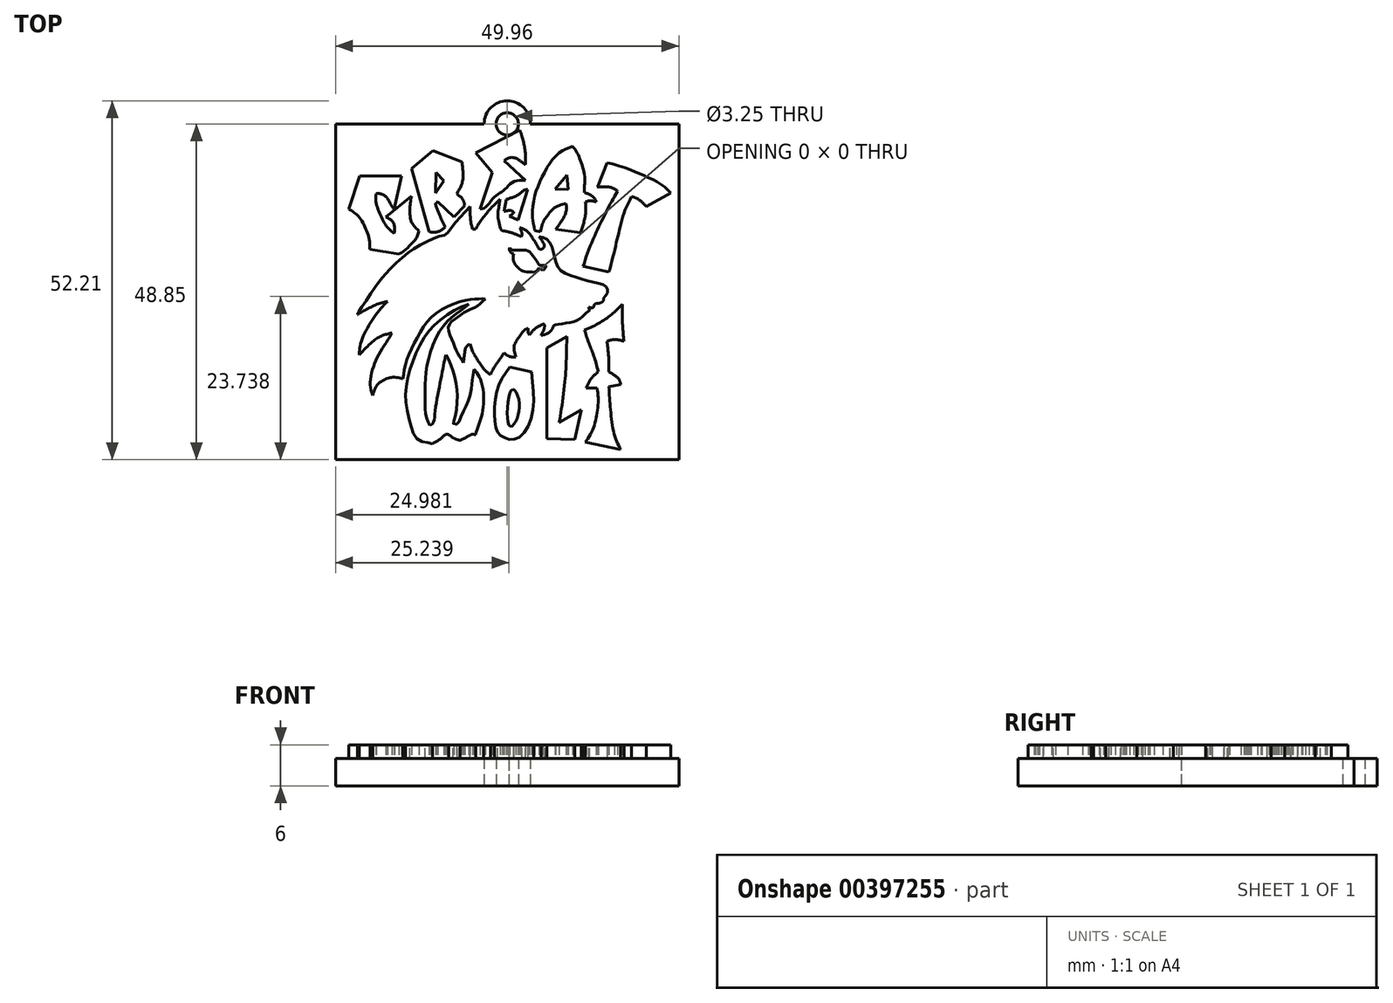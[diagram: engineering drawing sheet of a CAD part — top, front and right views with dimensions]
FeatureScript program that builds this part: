
annotation { "Feature Type Name" : "Feature", "Feature Type Description" : "" }
export const myFeature = defineFeature(function(context is Context, id is Id, definition is map)
    precondition{}
    {
        {
            var Q0;
            Q0=qCreatedBy(makeId("Top.planeOp"),FACE);
            var sketch = newSketch(context, id + "F0", { "sketchPlane" : qUnion([Q0])});
            skLineSegment(sketch, "E0", {"start": v(-47.52, 45.96) * mm, "end": v(-41.45, 45.96) * mm});
            skLineSegment(sketch, "E1", {"start": v(-47.52, 45.96) * mm, "end": v(-49.12, 41.16) * mm});
            skLineSegment(sketch, "E2", {"start": v(-41.45, 45.96) * mm, "end": v(-42.52, 41.16) * mm});
            skLineSegment(sketch, "E3", {"start": v(-43.72, 40.02) * mm, "end": v(-39.98, 43.03) * mm});
            skLineSegment(sketch, "E4", {"start": v(-46.05, 35.29) * mm, "end": v(-41.79, 34.62) * mm});
            skLineSegment(sketch, "E5", {"start": v(-39.98, 47.03) * mm, "end": v(-37.45, 37.89) * mm});
            skLineSegment(sketch, "E6", {"start": v(-36.45, 43.5) * mm, "end": v(-35.25, 45.3) * mm});
            skLineSegment(sketch, "E7", {"start": v(-35.25, 45.3) * mm, "end": v(-36.38, 46.5) * mm});
            skLineSegment(sketch, "E8", {"start": v(-36.38, 46.5) * mm, "end": v(-36.45, 43.5) * mm});
            skLineSegment(sketch, "E9", {"start": v(-33.78, 40.02) * mm, "end": v(-32.25, 41.7) * mm});
            skLineSegment(sketch, "E10", {"start": v(-33.78, 40.02) * mm, "end": v(-36.18, 42.23) * mm});
            skLineSegment(sketch, "E11", {"start": v(-28.24, 46.5) * mm, "end": v(-29.98, 41.16) * mm});
            skLineSegment(sketch, "E12", {"start": v(-28.24, 46.5) * mm, "end": v(-30.64, 49.36) * mm});
            skLineSegment(sketch, "E13", {"start": v(-30.64, 49.36) * mm, "end": v(-24.2, 52.66) * mm});
            skLineSegment(sketch, "E14", {"start": v(-19.05, 44.08) * mm, "end": v(-17.38, 46.1) * mm});
            skLineSegment(sketch, "E15", {"start": v(-17.38, 46.1) * mm, "end": v(-17.14, 44.04) * mm});
            skLineSegment(sketch, "E16", {"start": v(-17.14, 44.04) * mm, "end": v(-19.05, 44.08) * mm});
            skLineSegment(sketch, "E17", {"start": v(-11.51, 47.9) * mm, "end": v(-12.8, 44.65) * mm});
            skLineSegment(sketch, "E18", {"start": v(-5.8, 41.5) * mm, "end": v(-2.26, 43.5) * mm});
            skLineSegment(sketch, "E19", {"start": v(-15, 32.84) * mm, "end": v(-11.26, 32) * mm});
            skLineSegment(sketch, "E20", {"start": v(-20.3, 20.95) * mm, "end": v(-20.3, 7.77) * mm});
            skLineSegment(sketch, "E21", {"start": v(-18.49, 10.13) * mm, "end": v(-15.3, 11.92) * mm});
            skLineSegment(sketch, "E22", {"start": v(-15.3, 11.92) * mm, "end": v(-16.25, 7.63) * mm});
            skLineSegment(sketch, "E23", {"start": v(-20.3, 7.77) * mm, "end": v(-16.25, 7.63) * mm});
            skLineSegment(sketch, "E24", {"start": v(-20.3, 20.95) * mm, "end": v(-17.38, 22.59) * mm});
            skLineSegment(sketch, "E25", {"start": v(-25.7, 18.17) * mm, "end": v(-22.51, 17.47) * mm});
            skFitSpline(sketch, "E26", {"points": [v(-49.12, 41.16) * mm, v(-48.6, 40.84) * mm, v(-47.86, 40.25) * mm, v(-47.16, 39.38) * mm, v(-46.58, 38.18) * mm, v(-46.14, 36.9) * mm, v(-46.05, 35.29) * mm], "startDerivative": vector(4.18, -2.37) * mm, "endDerivative": vector(-0.07, -8.41) * mm});
            skFitSpline(sketch, "E27", {"points": [v(-43.72, 40.02) * mm, v(-43.17, 39.73) * mm, v(-42.79, 39.4) * mm, v(-42.5, 38.82) * mm, v(-42.44, 38.18) * mm, v(-42.5, 37.57) * mm], "startDerivative": vector(2.87, -1.43) * mm, "endDerivative": vector(-0.37, -3.02) * mm});
            skFitSpline(sketch, "E28", {"points": [v(-42.5, 37.57) * mm, v(-43.05, 38.04) * mm, v(-43.84, 39) * mm, v(-44.4, 40.02) * mm, v(-44.86, 41.16) * mm, v(-45.15, 42.35) * mm, v(-45.12, 43.4) * mm], "startDerivative": vector(-3.94, 3.01) * mm, "endDerivative": vector(0.59, 6.34) * mm});
            skFitSpline(sketch, "E29", {"points": [v(-45.12, 43.4) * mm, v(-44.54, 43.4) * mm, v(-43.9, 43.11) * mm, v(-43.37, 42.56) * mm, v(-42.93, 41.74) * mm, v(-42.52, 41.16) * mm], "startDerivative": vector(3.24, 0.32) * mm, "endDerivative": vector(2.17, -2.73) * mm});
            skFitSpline(sketch, "E30", {"points": [v(-39.98, 43.03) * mm, v(-40.15, 41.99) * mm, v(-40.22, 40.85) * mm, v(-40.1, 39.59) * mm, v(-39.82, 38.98) * mm, v(-39.31, 38.38) * mm, v(-38.92, 37.98) * mm], "startDerivative": vector(-0.98, -5.74) * mm, "endDerivative": vector(2.9, -2.79) * mm});
            skFitSpline(sketch, "E31", {"points": [v(-38.92, 37.98) * mm, v(-39.29, 36.91) * mm, v(-39.98, 36.12) * mm, v(-40.8, 35.29) * mm, v(-41.79, 34.62) * mm], "startDerivative": vector(-1.13, -4.54) * mm, "endDerivative": vector(-4.01, -2.4) * mm});
            skFitSpline(sketch, "E32", {"points": [v(-37.45, 37.89) * mm, v(-36.77, 37.78) * mm, v(-36.05, 37.89) * mm, v(-35.44, 38.23) * mm, v(-35.1, 38.56) * mm], "startDerivative": vector(2.6, -0.6) * mm, "endDerivative": vector(1.4, 1.59) * mm});
            skFitSpline(sketch, "E33", {"points": [v(-35.1, 38.56) * mm, v(-36.37, 41.46) * mm, v(-36.43, 41.98) * mm, v(-36.18, 42.23) * mm], "startDerivative": vector(-2.74, 6.01) * mm, "endDerivative": vector(1.6, 1.2) * mm});
            skFitSpline(sketch, "E34", {"points": [v(-32.25, 41.7) * mm, v(-32.5, 42.54) * mm, v(-32.96, 43.03) * mm, v(-33.41, 43.4) * mm], "startDerivative": vector(-0.5, 2.48) * mm, "endDerivative": vector(-1.47, 1.22) * mm});
            skFitSpline(sketch, "E35", {"points": [v(-33.41, 43.4) * mm, v(-33, 44.05) * mm, v(-32.54, 45.23) * mm, v(-32.5, 46.7) * mm, v(-32.62, 47.99) * mm], "startDerivative": vector(2.04, 2.95) * mm, "endDerivative": vector(-0.47, 4.8) * mm});
            skLineSegment(sketch, "E36", {"start": v(-32.62, 47.99) * mm, "end": v(-36.85, 49.65) * mm});
            skLineSegment(sketch, "E37", {"start": v(-36.85, 49.65) * mm, "end": v(-39.98, 47.03) * mm});
            skFitSpline(sketch, "E38", {"points": [v(-24.2, 52.66) * mm, v(-23.77, 51.24) * mm, v(-23.52, 50.1) * mm, v(-23.37, 48.64) * mm, v(-23.37, 47.62) * mm], "startDerivative": vector(1.77, -5.5) * mm, "endDerivative": vector(-0.11, -4.32) * mm});
            skFitSpline(sketch, "E39", {"points": [v(-23.37, 47.62) * mm, v(-24.2, 48.2) * mm, v(-24.84, 48.59) * mm, v(-25.73, 48.64) * mm, v(-26.51, 48.2) * mm], "startDerivative": vector(-3.26, 2.26) * mm, "endDerivative": vector(-2.94, -2.17) * mm});
            skFitSpline(sketch, "E40", {"points": [v(-26.51, 48.2) * mm, v(-23.37, 45.35) * mm], "startDerivative": vector(3.14, -2.84) * mm, "endDerivative": vector(3.14, -2.84) * mm});
            skFitSpline(sketch, "E41", {"points": [v(-23.37, 45.35) * mm, v(-25.14, 45.15) * mm, v(-26.27, 44.17) * mm, v(-27.15, 43.49) * mm, v(-28.03, 42.8) * mm, v(-29.16, 41.47) * mm, v(-29.98, 41.16) * mm], "startDerivative": vector(-9.9, 0.32) * mm, "endDerivative": vector(-6.05, -1.15) * mm});
            skFitSpline(sketch, "E42", {"points": [v(-23.08, 44.03) * mm, v(-24.45, 39.56) * mm], "startDerivative": vector(-1.37, -4.46) * mm, "endDerivative": vector(-1.37, -4.46) * mm});
            skFitSpline(sketch, "E43", {"points": [v(-24.45, 39.56) * mm, v(-25.73, 40.15) * mm], "startDerivative": vector(-1.28, 0.59) * mm, "endDerivative": vector(-1.28, 0.59) * mm});
            skFitSpline(sketch, "E44", {"points": [v(-25.73, 40.15) * mm, v(-25.1, 40.7) * mm, v(-25.53, 40.94) * mm, v(-26.51, 40.84) * mm], "startDerivative": vector(2.78, 1.66) * mm, "endDerivative": vector(-2.65, -0.57) * mm});
            skFitSpline(sketch, "E45", {"points": [v(-26.51, 40.84) * mm, v(-26.17, 42.55) * mm], "startDerivative": vector(0.34, 1.72) * mm, "endDerivative": vector(0.34, 1.72) * mm});
            skFitSpline(sketch, "E46", {"points": [v(-26.17, 42.55) * mm, v(-25.48, 42.8) * mm, v(-24.45, 43.24) * mm, v(-23.62, 43.88) * mm, v(-23.08, 44.03) * mm], "startDerivative": vector(2.78, 1.02) * mm, "endDerivative": vector(2.63, 0.33) * mm});
            skFitSpline(sketch, "E47", {"points": [v(-21.23, 37.82) * mm, v(-20.98, 38.77) * mm, v(-20.66, 39.56) * mm, v(-20.22, 40.15) * mm, v(-19.39, 41.16) * mm, v(-18.44, 41.7) * mm, v(-17.48, 41.95) * mm], "startDerivative": vector(1.44, 5.79) * mm, "endDerivative": vector(5.74, 1.3) * mm});
            skFitSpline(sketch, "E48", {"points": [v(-17.48, 41.95) * mm, v(-17.48, 40.84) * mm, v(-18.05, 39.56) * mm, v(-19, 38.2) * mm], "startDerivative": vector(0.38, -3.7) * mm, "endDerivative": vector(-2.74, -3.7) * mm});
            skFitSpline(sketch, "E49", {"points": [v(-19, 38.2) * mm, v(-15.38, 37.7) * mm], "startDerivative": vector(3.63, -0.5) * mm, "endDerivative": vector(3.63, -0.5) * mm});
            skFitSpline(sketch, "E50", {"points": [v(-15.38, 37.7) * mm, v(-14.94, 39.1) * mm, v(-14.62, 40.84) * mm, v(-14.68, 42.2) * mm], "startDerivative": vector(1.41, 4.1) * mm, "endDerivative": vector(-0.44, 4.18) * mm});
            skFitSpline(sketch, "E51", {"points": [v(-14.68, 42.2) * mm, v(-14.3, 42.32) * mm, v(-13.88, 42.37) * mm, v(-13.08, 42.2) * mm], "startDerivative": vector(1.3, 0.42) * mm, "endDerivative": vector(2.08, -0.56) * mm});
            skFitSpline(sketch, "E52", {"points": [v(-13.08, 42.2) * mm, v(-13.3, 42.67) * mm, v(-13.63, 43) * mm, v(-14.05, 43.26) * mm, v(-14.78, 43.57) * mm, v(-14.8, 43.57) * mm], "startDerivative": vector(-0.84, 2.1) * mm, "endDerivative": vector(-0.24, -0.08) * mm});
            skFitSpline(sketch, "E53", {"points": [v(-14.8, 43.57) * mm, v(-14.8, 44.58) * mm, v(-14.8, 46.09) * mm, v(-15.27, 47.87) * mm, v(-15.84, 49.27) * mm, v(-16.52, 50.29) * mm], "startDerivative": vector(-0.12, 5.66) * mm, "endDerivative": vector(-3.87, 5.2) * mm});
            skFitSpline(sketch, "E54", {"points": [v(-16.52, 50.29) * mm, v(-17.92, 49.72) * mm, v(-19.58, 48.2) * mm, v(-21.06, 45.6) * mm, v(-22.11, 42.8) * mm, v(-22.38, 40.38) * mm, v(-22.31, 39.36) * mm, v(-22.04, 38.01) * mm], "startDerivative": vector(-11.25, -3.54) * mm, "endDerivative": vector(2.66, -12.14) * mm});
            skFitSpline(sketch, "E55", {"points": [v(-22.04, 38.01) * mm, v(-21.23, 37.82) * mm], "startDerivative": vector(0.8, -0.2) * mm, "endDerivative": vector(0.8, -0.2) * mm});
            skFitSpline(sketch, "E56", {"points": [v(-11.51, 47.9) * mm, v(-10.38, 47.62) * mm, v(-8.35, 46.98) * mm, v(-5.93, 45.92) * mm, v(-3.66, 44.79) * mm, v(-2.26, 43.5) * mm], "startDerivative": vector(8.92, -1.3) * mm, "endDerivative": vector(6.59, -7.12) * mm});
            skFitSpline(sketch, "E57", {"points": [v(-5.8, 41.5) * mm, v(-6.47, 42.2) * mm, v(-7.3, 42.77) * mm, v(-7.94, 42.97) * mm], "startDerivative": vector(-1.81, 2.03) * mm, "endDerivative": vector(-2.13, 0.48) * mm});
            skFitSpline(sketch, "E58", {"points": [v(-7.94, 42.97) * mm, v(-8.56, 41.77) * mm, v(-9.05, 40.63) * mm, v(-9.52, 38.9) * mm, v(-9.87, 37.5) * mm, v(-10.22, 36.05) * mm, v(-10.72, 33.98) * mm, v(-11.26, 32) * mm], "startDerivative": vector(-4.88, -9.45) * mm, "endDerivative": vector(-3.42, -12.09) * mm});
            skFitSpline(sketch, "E59", {"points": [v(-15, 32.84) * mm, v(-14.2, 35.19) * mm, v(-13.08, 37.82) * mm, v(-12.24, 39.56) * mm, v(-11.26, 41.5) * mm, v(-10.46, 42.97) * mm], "startDerivative": vector(3.42, 10.76) * mm, "endDerivative": vector(4.46, 7.98) * mm});
            skFitSpline(sketch, "E60", {"points": [v(-10.46, 42.97) * mm, v(-9.97, 43.77) * mm], "startDerivative": vector(0.5, 0.8) * mm, "endDerivative": vector(0.5, 0.8) * mm});
            skFitSpline(sketch, "E61", {"points": [v(-9.97, 43.77) * mm, v(-10.64, 44.2) * mm, v(-11.51, 44.4) * mm, v(-12.19, 44.4) * mm, v(-12.95, 44.4) * mm], "startDerivative": vector(-2.47, 1.87) * mm, "endDerivative": vector(-3.18, 0.04) * mm});
            skFitSpline(sketch, "E62", {"points": [v(-12.95, 44.4) * mm, v(-12.8, 44.65) * mm], "startDerivative": vector(0.15, 0.25) * mm, "endDerivative": vector(0.15, 0.25) * mm});
            skFitSpline(sketch, "E63", {"points": [v(-34.98, 19.96) * mm, v(-34.09, 18.12) * mm, v(-33.45, 15.64) * mm, v(-33.32, 13.28) * mm, v(-33.7, 10.61) * mm, v(-33.9, 9.98) * mm, v(-33.39, 9.85) * mm, v(-32.75, 11) * mm, v(-31.86, 12.9) * mm, v(-31.29, 15.06) * mm, v(-30.9, 17.86) * mm, v(-30.9, 17.86) * mm], "startDerivative": vector(8.99, -16.5) * mm, "endDerivative": vector(0.47, -1.23) * mm});
            skFitSpline(sketch, "E64", {"points": [v(-30.9, 17.86) * mm, v(-30.2, 16.93) * mm, v(-29.53, 14.58) * mm, v(-29.64, 11.74) * mm, v(-30.17, 9.78) * mm, v(-30.66, 8.34) * mm], "startDerivative": vector(4.67, -5.16) * mm, "endDerivative": vector(-2.76, -7.91) * mm});
            skFitSpline(sketch, "E65", {"points": [v(-30.66, 8.34) * mm, v(-31.3, 8.34) * mm, v(-31.9, 8) * mm, v(-32.9, 7.5) * mm], "startDerivative": vector(-2.24, 0.28) * mm, "endDerivative": vector(-2.7, -1.22) * mm});
            skFitSpline(sketch, "E66", {"points": [v(-32.9, 7.5) * mm, v(-33.57, 7.7) * mm, v(-34.6, 8.34) * mm], "startDerivative": vector(-1.52, 0.28) * mm, "endDerivative": vector(-1.87, 1.33) * mm});
            skFitSpline(sketch, "E67", {"points": [v(-34.6, 8.34) * mm, v(-35.05, 8.34) * mm, v(-35.7, 7.77) * mm, v(-36.94, 7.02) * mm], "startDerivative": vector(-1.92, 0.38) * mm, "endDerivative": vector(-3.18, -1.62) * mm});
            skFitSpline(sketch, "E68", {"points": [v(-36.94, 7.02) * mm, v(-37.85, 7.2) * mm, v(-39.17, 7.7) * mm, v(-39.97, 9.32) * mm, v(-40.6, 11.93) * mm, v(-40.84, 14.4) * mm, v(-40.34, 17.23) * mm, v(-39.36, 20.14) * mm, v(-37.88, 22.83) * mm, v(-36.15, 24.72) * mm, v(-33.88, 26.38) * mm, v(-31.68, 27.29) * mm], "startDerivative": vector(-14.6, 3.12) * mm, "endDerivative": vector(23.86, 8.24) * mm});
            skFitSpline(sketch, "E69", {"points": [v(-31.68, 27.29) * mm, v(-33.5, 25.89) * mm, v(-35.54, 23.92) * mm, v(-37.4, 19.8) * mm, v(-37.96, 16.28) * mm, v(-38, 13.18) * mm, v(-37.81, 10.84) * mm, v(-37.29, 9.65) * mm], "startDerivative": vector(-13.78, -10.6) * mm, "endDerivative": vector(6.2, -11.05) * mm});
            skFitSpline(sketch, "E70", {"points": [v(-37.29, 9.65) * mm, v(-36.82, 10.03) * mm, v(-36.53, 11.75) * mm, v(-35.92, 15.33) * mm, v(-35.36, 18.2) * mm, v(-34.98, 19.96) * mm], "startDerivative": vector(4.81, 2.5) * mm, "endDerivative": vector(2, 8.8) * mm});
            skFitSpline(sketch, "E71", {"points": [v(-25.7, 18.17) * mm, v(-27.43, 15.12) * mm, v(-27.92, 11.1) * mm, v(-27.43, 8.7) * mm, v(-26.17, 7.76) * mm, v(-24.45, 7.86) * mm, v(-22.47, 11.1) * mm, v(-22.51, 17.47) * mm], "startDerivative": vector(-13.34, -18.9) * mm, "endDerivative": vector(-3.72, 33.09) * mm});
            skFitSpline(sketch, "E72", {"points": [v(-25.27, 14.92) * mm, v(-25.95, 13) * mm, v(-25.73, 9.65) * mm, v(-25.27, 9.65) * mm, v(-24.45, 11.2) * mm, v(-24.45, 13.8) * mm, v(-25.27, 14.92) * mm]});
            skFitSpline(sketch, "E73", {"points": [v(-18.49, 10.13) * mm, v(-18.05, 12.73) * mm, v(-17.64, 16.2) * mm, v(-17.48, 18.7) * mm, v(-17.38, 22.59) * mm], "startDerivative": vector(1.9, 10.65) * mm, "endDerivative": vector(0.34, 14.9) * mm});
            skFitSpline(sketch, "E74", {"points": [v(-14.68, 7.22) * mm, v(-9.52, 6.14) * mm], "startDerivative": vector(5.16, -1.08) * mm, "endDerivative": vector(5.16, -1.08) * mm});
            skFitSpline(sketch, "E75", {"points": [v(-9.52, 6.14) * mm, v(-10.46, 8.34) * mm, v(-11.02, 12.03) * mm, v(-11.26, 15.31) * mm], "startDerivative": vector(-3.56, 6.88) * mm, "endDerivative": vector(-0.58, 9.26) * mm});
            skFitSpline(sketch, "E76", {"points": [v(-11.26, 15.31) * mm, v(-9.52, 15.65) * mm], "startDerivative": vector(1.74, 0.34) * mm, "endDerivative": vector(1.74, 0.34) * mm});
            skFitSpline(sketch, "E77", {"points": [v(-9.52, 15.65) * mm, v(-9.87, 16.49) * mm, v(-11.26, 17.47) * mm], "startDerivative": vector(-0.5, 2.04) * mm, "endDerivative": vector(-2.85, 1.6) * mm});
            skFitSpline(sketch, "E78", {"points": [v(-11.26, 17.47) * mm, v(-11.26, 19.04) * mm, v(-11.51, 21.93) * mm], "startDerivative": vector(0.1, 3.43) * mm, "endDerivative": vector(-0.58, 5.4) * mm});
            skFitSpline(sketch, "E79", {"points": [v(-11.51, 21.93) * mm, v(-10.46, 22.18) * mm, v(-9.06, 21.93) * mm], "startDerivative": vector(2.18, 0.76) * mm, "endDerivative": vector(2.72, -0.72) * mm});
            skFitSpline(sketch, "E80", {"points": [v(-9.06, 21.93) * mm, v(-9.2, 23.39) * mm, v(-9.29, 25.1) * mm, v(-9.32, 27.29) * mm], "startDerivative": vector(-0.52, 4.74) * mm, "endDerivative": vector(-0.04, 6.06) * mm});
            skFitSpline(sketch, "E81", {"points": [v(-9.32, 27.29) * mm, v(-10.31, 26.3) * mm, v(-11.51, 25.31) * mm, v(-12.95, 24.4) * mm, v(-14.8, 23.6) * mm], "startDerivative": vector(-4.19, -4.33) * mm, "endDerivative": vector(-6.92, -2.83) * mm});
            skFitSpline(sketch, "E82", {"points": [v(-14.8, 23.6) * mm, v(-14.2, 21.75) * mm, v(-13.5, 19.96) * mm, v(-12.8, 17.47) * mm], "startDerivative": vector(1.75, -5.9) * mm, "endDerivative": vector(1.77, -7.14) * mm});
            skFitSpline(sketch, "E83", {"points": [v(-12.8, 17.47) * mm, v(-13.75, 16.6) * mm, v(-14.55, 15.11) * mm], "startDerivative": vector(-2.14, -1.64) * mm, "endDerivative": vector(-1.37, -3.03) * mm});
            skFitSpline(sketch, "E84", {"points": [v(-14.55, 15.11) * mm, v(-12.95, 15.11) * mm], "startDerivative": vector(1.6, 0) * mm, "endDerivative": vector(1.6, 0) * mm});
            skFitSpline(sketch, "E85", {"points": [v(-12.95, 15.11) * mm, v(-12.8, 13.13) * mm, v(-13.08, 10.92) * mm, v(-13.72, 8.81) * mm, v(-14.68, 7.22) * mm], "startDerivative": vector(0.96, -7.98) * mm, "endDerivative": vector(-4.39, -6.38) * mm});
            skFitSpline(sketch, "E86", {"points": [v(-43.47, 27.71) * mm, v(-45, 27.29) * mm, v(-46.59, 26.54) * mm, v(-47.67, 25.93) * mm, v(-47.84, 25.76) * mm], "startDerivative": vector(-5.1, -1.18) * mm, "endDerivative": vector(-1.05, -1.37) * mm});
            skFitSpline(sketch, "E87", {"points": [v(-47.84, 25.76) * mm, v(-47.6, 26.32) * mm, v(-46.63, 27.78) * mm, v(-44.96, 30.19) * mm, v(-43.34, 32.21) * mm, v(-41.4, 34.06) * mm, v(-39.63, 35.36) * mm, v(-37.53, 36.56) * mm, v(-35.85, 37.22) * mm, v(-34.98, 37.42) * mm, v(-34.19, 38.43) * mm, v(-32.9, 40) * mm, v(-31.45, 41.5) * mm], "startDerivative": vector(4, 10.75) * mm, "endDerivative": vector(16.43, 16.99) * mm});
            skFitSpline(sketch, "E88", {"points": [v(-31.45, 41.5) * mm, v(-31.45, 40.84) * mm, v(-31.36, 39.37) * mm, v(-31.08, 38.2) * mm], "startDerivative": vector(-0.02, -2.27) * mm, "endDerivative": vector(0.92, -3.12) * mm});
            skFitSpline(sketch, "E89", {"points": [v(-31.08, 38.2) * mm, v(-30.66, 38.2) * mm], "startDerivative": vector(0.42, 0) * mm, "endDerivative": vector(0.42, 0) * mm});
            skFitSpline(sketch, "E90", {"points": [v(-30.66, 38.2) * mm, v(-30.16, 39.09) * mm, v(-28.81, 40.84) * mm, v(-27.08, 42.63) * mm], "startDerivative": vector(1.68, 3.31) * mm, "endDerivative": vector(4.55, 4.47) * mm});
            skFitSpline(sketch, "E91", {"points": [v(-27.08, 42.63) * mm, v(-27.27, 41.5) * mm, v(-27.42, 40.39) * mm, v(-27.39, 39.92) * mm, v(-26.96, 38.2) * mm, v(-26.76, 38.01) * mm], "startDerivative": vector(-0.82, -4.67) * mm, "endDerivative": vector(1.68, -0.85) * mm});
            skFitSpline(sketch, "E92", {"points": [v(-26.76, 38.01) * mm, v(-26.17, 37.9) * mm, v(-25.27, 37.67) * mm, v(-24.04, 37.15) * mm], "startDerivative": vector(2.12, -0.33) * mm, "endDerivative": vector(3.15, -1.45) * mm});
            skFitSpline(sketch, "E93", {"points": [v(-24.04, 37.15) * mm, v(-23.89, 37.42) * mm, v(-24.2, 38.45) * mm], "startDerivative": vector(0.6, 0.65) * mm, "endDerivative": vector(-0.8, 1.84) * mm});
            skFitSpline(sketch, "E94", {"points": [v(-24.2, 38.45) * mm, v(-23.37, 38.1) * mm, v(-22.41, 37.02) * mm, v(-21.42, 35.38) * mm], "startDerivative": vector(3.15, -0.9) * mm, "endDerivative": vector(2.45, -4.35) * mm});
            skFitSpline(sketch, "E95", {"points": [v(-21.42, 35.38) * mm, v(-21.02, 35.3) * mm, v(-20.66, 35.8) * mm, v(-21.42, 37.15) * mm], "startDerivative": vector(1.64, -0.7) * mm, "endDerivative": vector(-2.52, 3.11) * mm});
            skFitSpline(sketch, "E96", {"points": [v(-21.42, 37.15) * mm, v(-20.3, 36.79) * mm, v(-19.47, 35.38) * mm, v(-19, 33.5) * mm, v(-18.22, 32.17) * mm, v(-16.18, 31.3) * mm, v(-14.02, 30.62) * mm, v(-12.02, 30.13) * mm, v(-11.51, 29.56) * mm, v(-11.51, 28.84) * mm, v(-11.98, 28.24) * mm, v(-12.06, 27.86) * mm, v(-12.59, 27.48) * mm, v(-13.34, 27.29) * mm, v(-13.57, 26.83) * mm, v(-14.2, 26.83) * mm, v(-14.06, 26.54) * mm, v(-14.55, 26.05) * mm, v(-15.42, 25.21) * mm, v(-17.38, 24.57) * mm, v(-19.17, 24.23) * mm, v(-19.4, 23.93) * mm, v(-19.85, 23.28) * mm, v(-20.87, 22.83) * mm, v(-21.12, 22.83) * mm], "startDerivative": vector(26.73, -3.85) * mm, "endDerivative": vector(-9.64, 1.43) * mm});
            skFitSpline(sketch, "E97", {"points": [v(-21.12, 22.83) * mm, v(-20.94, 23.15) * mm, v(-20.66, 23.83) * mm, v(-20.66, 24.37) * mm, v(-20.78, 24.46) * mm], "startDerivative": vector(0.7, 1.25) * mm, "endDerivative": vector(-0.92, 0.37) * mm});
            skFitSpline(sketch, "E98", {"points": [v(-20.78, 24.46) * mm, v(-21.23, 24.21) * mm, v(-22.04, 23.72) * mm, v(-22.83, 22.83) * mm], "startDerivative": vector(-1.6, -0.9) * mm, "endDerivative": vector(-1.88, -2.47) * mm});
            skFitSpline(sketch, "E99", {"points": [v(-22.83, 22.83) * mm, v(-22.99, 23.15) * mm, v(-22.99, 23.6) * mm, v(-22.99, 23.94) * mm], "startDerivative": vector(-0.6, 0.94) * mm, "endDerivative": vector(-0.03, 1.05) * mm});
            skFitSpline(sketch, "E100", {"points": [v(-22.98, 23.83) * mm, v(-23.66, 23.42) * mm, v(-24.45, 22.35) * mm, v(-25.06, 21.12) * mm, v(-24.77, 19.63) * mm], "startDerivative": vector(-3.47, -1.55) * mm, "endDerivative": vector(1.93, -5.57) * mm});
            skFitSpline(sketch, "E101", {"points": [v(-24.77, 19.63) * mm, v(-25.27, 19.63) * mm, v(-25.93, 19.8) * mm, v(-26.51, 20.25) * mm], "startDerivative": vector(-1.62, -0.08) * mm, "endDerivative": vector(-1.53, 1.39) * mm});
            skFitSpline(sketch, "E102", {"points": [v(-26.51, 20.25) * mm, v(-27.08, 19.4) * mm, v(-27.8, 18.35) * mm, v(-28.5, 17.1) * mm], "startDerivative": vector(-1.79, -2.75) * mm, "endDerivative": vector(-1.88, -3.58) * mm});
            skFitSpline(sketch, "E103", {"points": [v(-28.5, 17.1) * mm, v(-29.17, 17.6) * mm, v(-30.16, 18.9) * mm, v(-31.08, 20.4) * mm], "startDerivative": vector(-2.54, 1.55) * mm, "endDerivative": vector(-2.36, 3.92) * mm});
            skFitSpline(sketch, "E104", {"points": [v(-31.08, 20.4) * mm, v(-31.45, 21.51) * mm], "startDerivative": vector(-0.36, 1.12) * mm, "endDerivative": vector(-0.36, 1.12) * mm});
            skFitSpline(sketch, "E105", {"points": [v(-31.45, 21.51) * mm, v(-31.98, 21.14) * mm, v(-32.28, 19.96) * mm, v(-32.41, 18.83) * mm], "startDerivative": vector(-2.23, -0.96) * mm, "endDerivative": vector(-0.36, -3.02) * mm});
            skFitSpline(sketch, "E106", {"points": [v(-32.41, 18.83) * mm, v(-33.27, 20.25) * mm, v(-34.03, 21.93) * mm, v(-34.6, 24.05) * mm, v(-33.76, 25.07) * mm, v(-32.06, 26.24) * mm, v(-30.43, 27.04) * mm, v(-29.22, 28.1) * mm], "startDerivative": vector(-6.54, 10.16) * mm, "endDerivative": vector(8.31, 8.51) * mm});
            skFitSpline(sketch, "E107", {"points": [v(-29.22, 28.1) * mm, v(-30.43, 28.1) * mm, v(-32.9, 27.68) * mm, v(-36.94, 25.56) * mm, v(-39.25, 22.27) * mm, v(-40.8, 18.83) * mm, v(-41.22, 16.45) * mm], "startDerivative": vector(-10.55, 0.3) * mm, "endDerivative": vector(-2.6, -14.41) * mm});
            skFitSpline(sketch, "E108", {"points": [v(-41.22, 16.45) * mm, v(-42.64, 16.68) * mm, v(-43.63, 16.45) * mm, v(-44.88, 15.65) * mm, v(-45.64, 14.06) * mm], "startDerivative": vector(-4.26, 1.98) * mm, "endDerivative": vector(-2.22, -6.17) * mm});
            skFitSpline(sketch, "E109", {"points": [v(-45.64, 14.06) * mm, v(-45.98, 15.65) * mm, v(-45.64, 17.86) * mm, v(-44.58, 20.25) * mm, v(-43.26, 22.38) * mm, v(-42.8, 23.14) * mm], "startDerivative": vector(-2.53, 8.23) * mm, "endDerivative": vector(2.8, 4.85) * mm});
            skFitSpline(sketch, "E110", {"points": [v(-42.8, 23.14) * mm, v(-43.97, 22.83) * mm, v(-45.34, 22.12) * mm, v(-47.57, 19.96) * mm], "startDerivative": vector(-4.37, -1) * mm, "endDerivative": vector(-5.4, -5.75) * mm});
            skFitSpline(sketch, "E111", {"points": [v(-47.57, 19.96) * mm, v(-47.42, 21.51) * mm, v(-46.4, 23.83) * mm, v(-44.73, 26.35) * mm, v(-43.47, 27.71) * mm], "startDerivative": vector(0.1, 7.12) * mm, "endDerivative": vector(5.39, 5.32) * mm});
            skFitSpline(sketch, "E112", {"points": [v(-29.22, 28.1) * mm, v(-27.77, 28.41) * mm, v(-25.7, 28.48) * mm, v(-25.7, 28.48) * mm], "startDerivative": vector(2.52, 0.84) * mm, "endDerivative": vector(-0.05, -0.08) * mm});
            skFitSpline(sketch, "E113", {"points": [v(-25.7, 28.48) * mm, v(-25.87, 28.68) * mm, v(-26.65, 29.17) * mm], "startDerivative": vector(-0.35, 0.56) * mm, "endDerivative": vector(-1.43, 0.8) * mm});
            skFitSpline(sketch, "E114", {"points": [v(-26.65, 29.17) * mm, v(-26.06, 29.55) * mm, v(-24.04, 30.26) * mm, v(-21.53, 30.9) * mm, v(-18.8, 30.75) * mm, v(-16.78, 30.31) * mm, v(-15.97, 29.67) * mm], "startDerivative": vector(4.63, 3.62) * mm, "endDerivative": vector(5.45, -5.6) * mm});
            skFitSpline(sketch, "E115", {"points": [v(-15.97, 29.67) * mm, v(-15.15, 29.67) * mm, v(-14.1, 29.76) * mm, v(-13.28, 29.67) * mm, v(-12.67, 29.17) * mm, v(-12.3, 28.37) * mm, v(-12.36, 27.87) * mm, v(-12.06, 27.86) * mm], "startDerivative": vector(5.13, -0.16) * mm, "endDerivative": vector(4.24, 0.8) * mm});
            skFitSpline(sketch, "E116", {"points": [v(-14.2, 26.83) * mm, v(-15.42, 27.04) * mm, v(-16.24, 27.29) * mm, v(-17.87, 27.48) * mm, v(-19.38, 27.48) * mm, v(-21.02, 27.48) * mm, v(-22.98, 26.83) * mm], "startDerivative": vector(-8.6, 1.13) * mm, "endDerivative": vector(-10.02, -4.21) * mm});
            skFitSpline(sketch, "E117", {"points": [v(-22.98, 26.83) * mm, v(-22.67, 27.86) * mm, v(-21.76, 29.17) * mm, v(-20.4, 29.67) * mm, v(-18.05, 29.4) * mm, v(-16.2, 28.48) * mm, v(-14.68, 27.29) * mm, v(-13.34, 27.29) * mm], "startDerivative": vector(1.99, 8.57) * mm, "endDerivative": vector(10.65, 1.96) * mm});
            skFitSpline(sketch, "E118", {"points": [v(-20.36, 32.96) * mm, v(-21.02, 33) * mm, v(-21.42, 33.05) * mm, v(-21.74, 33.54) * mm, v(-22.26, 34.27) * mm, v(-22.98, 35.06) * mm, v(-23.8, 35.19) * mm, v(-24.77, 35.19) * mm, v(-25.27, 35.19) * mm, v(-25.7, 35.5) * mm], "startDerivative": vector(-6.38, 0.44) * mm, "endDerivative": vector(-4.36, 4.1) * mm});
            skFitSpline(sketch, "E119", {"points": [v(-25.7, 35.5) * mm, v(-25.73, 35.24) * mm, v(-25.59, 34.95) * mm, v(-25.27, 34.67) * mm, v(-24.9, 34.68) * mm, v(-24.04, 34.63) * mm, v(-23.08, 34.3) * mm, v(-22.51, 33.63) * mm, v(-22.04, 32.9) * mm, v(-21.54, 32.64) * mm, v(-21.12, 32.38) * mm, v(-20.74, 32.32) * mm, v(-20.36, 32.96) * mm], "startDerivative": vector(-1.04, -4.56) * mm, "endDerivative": vector(3.37, 8.97) * mm});
            skFitSpline(sketch, "E120", {"points": [v(-21.42, 32.57) * mm, v(-21.67, 32.29) * mm, v(-22, 32) * mm, v(-22.51, 32) * mm, v(-23.6, 32.07) * mm, v(-24.45, 32.62) * mm, v(-25.12, 33.57) * mm, v(-25.12, 34.65) * mm], "startDerivative": vector(-2.4, -2.72) * mm, "endDerivative": vector(0.93, 6.57) * mm});
            skLineSegment(sketch, "E121.bottom", {"start": v(-50.94, 53.6) * mm, "end": v(-0.98, 53.6) * mm});
            skLineSegment(sketch, "E121.top", {"start": v(-50.94, 4.74) * mm, "end": v(-0.98, 4.74) * mm});
            skLineSegment(sketch, "E121.left", {"start": v(-50.94, 53.6) * mm, "end": v(-50.94, 4.74) * mm});
            skLineSegment(sketch, "E121.right", {"start": v(-0.98, 53.6) * mm, "end": v(-0.98, 4.74) * mm});
            skPoint(sketch, "E122", {"position": v(-25.96, 53.6) * mm});
            skCircle(sketch, "E123", {"center": v(-25.96, 53.6) * mm, "radius": 1.63 * mm});
            skCircle(sketch, "E124", {"center": v(-25.96, 53.6) * mm, "radius": 3.35 * mm});
            skSolve(sketch);
        }
        {
            var Q0;
            Q0=makeQuery(id+"F0.imprint","IMPRINT",FACE,{"disambiguationData":[TD([[makeQuery(id+"F0.imprint","IMPRINT",EDGE,{"derivedFrom":sQuery(id+"F0.wireOp",EDGE,"E0")}),1.0]])]});
            var Q1;
            Q1=makeQuery(id+"F0.imprint","IMPRINT",FACE,{"disambiguationData":[TD([[makeQuery(id+"F0.imprint","IMPRINT",EDGE,{"derivedFrom":sQuery(id+"F0.wireOp",EDGE,"E0")}),-1.0]])]});
            var Q2;
            Q2=makeQuery(id+"F0.imprint","IMPRINT",FACE,{"disambiguationData":[TD([[makeQuery(id+"F0.imprint","IMPRINT",EDGE,{"derivedFrom":sQuery(id+"F0.wireOp",EDGE,"E5")}),1.0]])]});
            var Q3;
            Q3=makeQuery(id+"F0.imprint","IMPRINT",FACE,{"disambiguationData":[TD([[makeQuery(id+"F0.imprint","IMPRINT",EDGE,{"derivedFrom":sQuery(id+"F0.wireOp",EDGE,"E6")}),1.0]])]});
            var Q4;
            Q4=makeQuery(id+"F0.imprint","IMPRINT",FACE,{"disambiguationData":[TD([[makeQuery(id+"F0.imprint","IMPRINT",EDGE,{"derivedFrom":sQuery(id+"F0.wireOp",EDGE,"E11")}),1.0]])]});
            var Q5;
            Q5=makeQuery(id+"F0.imprint","IMPRINT",FACE,{"disambiguationData":[TD([[makeQuery(id+"F0.imprint","IMPRINT",EDGE,{"derivedFrom":sQuery(id+"F0.wireOp",EDGE,"E42")}),-1.0]])]});
            var Q6;
            Q6=makeQuery(id+"F0.imprint","IMPRINT",FACE,{"disambiguationData":[TD([[makeQuery(id+"F0.imprint","IMPRINT",EDGE,{"derivedFrom":sQuery(id+"F0.wireOp",EDGE,"E14")}),1.0]])]});
            var Q7;
            Q7=makeQuery(id+"F0.imprint","IMPRINT",FACE,{"disambiguationData":[TD([[makeQuery(id+"F0.imprint","IMPRINT",EDGE,{"derivedFrom":sQuery(id+"F0.wireOp",EDGE,"E14")}),-1.0]])]});
            var Q8;
            Q8=makeQuery(id+"F0.imprint","IMPRINT",FACE,{"disambiguationData":[TD([[makeQuery(id+"F0.imprint","IMPRINT",EDGE,{"derivedFrom":sQuery(id+"F0.wireOp",EDGE,"E17")}),1.0]])]});
            var Q9;
            Q9=makeQuery(id+"F0.imprint","IMPRINT",FACE,{"disambiguationData":[TD([[makeQuery(id+"F0.imprint","IMPRINT",EDGE,{"derivedFrom":sQuery(id+"F0.wireOp",EDGE,"E86")}),-1.0]])]});
            var Q10;
            {var subQ8=sQuery(id+"F0.wireOp",EDGE,"E97");Q10=makeQuery(id+"F0.imprint","IMPRINT",FACE,{"disambiguationData":[TD([[makeQuery(id+"F0.imprint","IMPRINT",EDGE,{"derivedFrom":subQ8}),-1.0]])]});}
            var Q11;
            {var subQ0=sQuery(id+"F0.wireOp",EDGE,"E116");Q11=makeQuery(id+"F0.imprint","IMPRINT",FACE,{"disambiguationData":[TD([[makeQuery(id+"F0.imprint","IMPRINT",EDGE,{"derivedFrom":subQ0}),-1.0]])]});}
            var Q12;
            {var subQ0=sQuery(id+"F0.wireOp",EDGE,"E120");Q12=makeQuery(id+"F0.imprint","IMPRINT",FACE,{"disambiguationData":[TD([[makeQuery(id+"F0.imprint","IMPRINT",EDGE,{"derivedFrom":subQ0}),-1.0]])]});}
            var Q13;
            {var subQ0=sQuery(id+"F0.wireOp",EDGE,"E118");Q13=makeQuery(id+"F0.imprint","IMPRINT",FACE,{"disambiguationData":[TD([[makeQuery(id+"F0.imprint","IMPRINT",EDGE,{"derivedFrom":subQ0}),1.0]])]});}
            var Q14;
            Q14=makeQuery(id+"F0.imprint","IMPRINT",FACE,{"disambiguationData":[TD([[makeQuery(id+"F0.imprint","IMPRINT",EDGE,{"derivedFrom":sQuery(id+"F0.wireOp",EDGE,"E20")}),1.0]])]});
            var Q15;
            Q15=makeQuery(id+"F0.imprint","IMPRINT",FACE,{"disambiguationData":[TD([[makeQuery(id+"F0.imprint","IMPRINT",EDGE,{"derivedFrom":sQuery(id+"F0.wireOp",EDGE,"E25")}),-1.0]])]});
            var Q16;
            Q16=makeQuery(id+"F0.imprint","IMPRINT",FACE,{"disambiguationData":[TD([[makeQuery(id+"F0.imprint","IMPRINT",EDGE,{"derivedFrom":sQuery(id+"F0.wireOp",EDGE,"E72")}),1.0]])]});
            var Q17;
            Q17=makeQuery(id+"F0.imprint","IMPRINT",FACE,{"disambiguationData":[TD([[makeQuery(id+"F0.imprint","IMPRINT",EDGE,{"derivedFrom":sQuery(id+"F0.wireOp",EDGE,"E63")}),-1.0]])]});
            var Q18;
            Q18=makeQuery(id+"F0.imprint","IMPRINT",FACE,{"disambiguationData":[TD([[makeQuery(id+"F0.imprint","IMPRINT",EDGE,{"derivedFrom":sQuery(id+"F0.wireOp",EDGE,"E74")}),1.0]])]});
            var Q19;
            {var subQ0=sQuery(id+"F0.wireOp",EDGE,"E124");var subQ1=sQuery(id+"F0.wireOp",EDGE,"E121.bottom");var subQ2=makeQuery(id+"F0.imprint","INTERSECT",VERTEX,{"disambiguationData":[OD(0.0)],"derivedFrom":[subQ1,subQ0]});Q19=makeQuery(id+"F0.imprint","IMPRINT",FACE,{"disambiguationData":[TD([[makeQuery(id+"F0.imprint","IMPRINT",EDGE,{"disambiguationData":[TD([[subQ2,-1.0]])],"derivedFrom":subQ1}),1.0]])]});}
            var Q20;
            {var subQ0=sQuery(id+"F0.wireOp",EDGE,"E124");var subQ1=sQuery(id+"F0.wireOp",EDGE,"E13");var subQ2=makeQuery(id+"F0.imprint","INTERSECT",VERTEX,{"derivedFrom":[subQ1,subQ0]});Q20=makeQuery(id+"F0.imprint","IMPRINT",FACE,{"disambiguationData":[TD([[makeQuery(id+"F0.imprint","IMPRINT",EDGE,{"disambiguationData":[TD([[subQ2,-1.0]])],"derivedFrom":subQ1}),1.0]])]});}
            var Q21;
            {var subQ0=sQuery(id+"F0.wireOp",EDGE,"E124");var subQ1=sQuery(id+"F0.wireOp",EDGE,"E13");var subQ2=makeQuery(id+"F0.imprint","INTERSECT",VERTEX,{"derivedFrom":[subQ1,subQ0]});Q21=makeQuery(id+"F0.imprint","IMPRINT",FACE,{"disambiguationData":[TD([[makeQuery(id+"F0.imprint","IMPRINT",EDGE,{"disambiguationData":[TD([[subQ2,-1.0]])],"derivedFrom":subQ1}),-1.0]])]});}
            var Q22;
            {var subQ1=sQuery(id+"F0.wireOp",EDGE,"E13");var subQ5=sQuery(id+"F0.wireOp",EDGE,"E38");var subQ6=makeQuery(id+"F0.imprint","INTERSECT",VERTEX,{"derivedFrom":[subQ1,subQ5]});Q22=makeQuery(id+"F0.imprint","IMPRINT",FACE,{"disambiguationData":[TD([[makeQuery(id+"F0.imprint","IMPRINT",EDGE,{"disambiguationData":[TD([[subQ6,1.0]])],"derivedFrom":subQ1}),1.0]])]});}
            extrude(context, id + "F1", {"entities" : qUnion([Q0, Q1, Q2, Q3, Q4, Q5, Q6, Q7, Q8, Q9, Q10, Q11, Q12, Q13, Q14, Q15, Q16, Q17, Q18, Q19, Q20, Q21, Q22]), "depth" : 4 * mm});
        }
        {
            var Q0;
            Q0=makeQuery(id+"F1.opExtrude","CAP_FACE",FACE,{"disambiguationData":[OSD([sQuery(id+"F0.wireOp",EDGE,"E121.bottom"),sQuery(id+"F0.wireOp",EDGE,"E121.top"),sQuery(id+"F0.wireOp",EDGE,"E121.left"),sQuery(id+"F0.wireOp",EDGE,"E121.right")])],"isStart":false});
            var sketch = newSketch(context, id + "F2", { "sketchPlane" : qUnion([Q0])});
            skLineSegment(sketch, "E125", {"start": v(-47.43, 46) * mm, "end": v(-41.36, 46) * mm});
            skLineSegment(sketch, "E126", {"start": v(-47.43, 46) * mm, "end": v(-49.03, 41.2) * mm});
            skLineSegment(sketch, "E127", {"start": v(-41.36, 46) * mm, "end": v(-42.43, 41.2) * mm});
            skLineSegment(sketch, "E128", {"start": v(-43.63, 40.06) * mm, "end": v(-39.9, 43.06) * mm});
            skLineSegment(sketch, "E129", {"start": v(-45.96, 35.32) * mm, "end": v(-41.7, 34.66) * mm});
            skLineSegment(sketch, "E130", {"start": v(-39.9, 47.07) * mm, "end": v(-37.36, 37.93) * mm});
            skLineSegment(sketch, "E131", {"start": v(-36.36, 43.53) * mm, "end": v(-35.15, 45.33) * mm});
            skLineSegment(sketch, "E132", {"start": v(-35.15, 45.33) * mm, "end": v(-36.29, 46.53) * mm});
            skLineSegment(sketch, "E133", {"start": v(-36.29, 46.53) * mm, "end": v(-36.36, 43.53) * mm});
            skLineSegment(sketch, "E134", {"start": v(-33.69, 40.06) * mm, "end": v(-32.15, 41.73) * mm});
            skLineSegment(sketch, "E135", {"start": v(-33.69, 40.06) * mm, "end": v(-36.1, 42.27) * mm});
            skLineSegment(sketch, "E136", {"start": v(-28.15, 46.53) * mm, "end": v(-29.88, 41.2) * mm});
            skLineSegment(sketch, "E137", {"start": v(-28.15, 46.53) * mm, "end": v(-30.55, 49.4) * mm});
            skLineSegment(sketch, "E138", {"start": v(-30.55, 49.4) * mm, "end": v(-24.11, 52.7) * mm});
            skLineSegment(sketch, "E139", {"start": v(-18.96, 44.11) * mm, "end": v(-17.28, 46.14) * mm});
            skLineSegment(sketch, "E140", {"start": v(-17.28, 46.14) * mm, "end": v(-17.05, 44.07) * mm});
            skLineSegment(sketch, "E141", {"start": v(-17.05, 44.07) * mm, "end": v(-18.96, 44.11) * mm});
            skLineSegment(sketch, "E142", {"start": v(-11.42, 47.93) * mm, "end": v(-12.71, 44.68) * mm});
            skLineSegment(sketch, "E143", {"start": v(-14.91, 32.87) * mm, "end": v(-11.16, 32.04) * mm});
            skLineSegment(sketch, "E144", {"start": v(-20.2, 20.99) * mm, "end": v(-20.2, 7.8) * mm});
            skLineSegment(sketch, "E145", {"start": v(-18.4, 10.16) * mm, "end": v(-15.2, 11.96) * mm});
            skLineSegment(sketch, "E146", {"start": v(-15.2, 11.96) * mm, "end": v(-16.15, 7.66) * mm});
            skLineSegment(sketch, "E147", {"start": v(-20.2, 7.8) * mm, "end": v(-16.15, 7.66) * mm});
            skLineSegment(sketch, "E148", {"start": v(-20.2, 20.99) * mm, "end": v(-17.28, 22.62) * mm});
            skLineSegment(sketch, "E149", {"start": v(-25.6, 18.21) * mm, "end": v(-22.42, 17.5) * mm});
            skFitSpline(sketch, "E150", {"points": [v(-49.03, 41.2) * mm, v(-48.5, 40.87) * mm, v(-47.77, 40.3) * mm, v(-47.07, 39.42) * mm, v(-46.49, 38.22) * mm, v(-46.05, 36.94) * mm, v(-45.96, 35.32) * mm], "startDerivative": vector(4.18, -2.37) * mm, "endDerivative": vector(-0.07, -8.41) * mm});
            skFitSpline(sketch, "E151", {"points": [v(-43.63, 40.06) * mm, v(-43.07, 39.77) * mm, v(-42.7, 39.44) * mm, v(-42.4, 38.86) * mm, v(-42.34, 38.22) * mm, v(-42.4, 37.6) * mm], "startDerivative": vector(2.87, -1.43) * mm, "endDerivative": vector(-0.37, -3.02) * mm});
            skFitSpline(sketch, "E152", {"points": [v(-42.4, 37.6) * mm, v(-42.96, 38.07) * mm, v(-43.74, 39.04) * mm, v(-44.3, 40.06) * mm, v(-44.77, 41.2) * mm, v(-45.06, 42.4) * mm, v(-45.03, 43.44) * mm], "startDerivative": vector(-3.94, 3.01) * mm, "endDerivative": vector(0.59, 6.34) * mm});
            skFitSpline(sketch, "E153", {"points": [v(-45.03, 43.44) * mm, v(-44.44, 43.44) * mm, v(-43.8, 43.15) * mm, v(-43.28, 42.6) * mm, v(-42.84, 41.78) * mm, v(-42.43, 41.2) * mm], "startDerivative": vector(3.24, 0.32) * mm, "endDerivative": vector(2.17, -2.73) * mm});
            skFitSpline(sketch, "E154", {"points": [v(-39.9, 43.06) * mm, v(-40.05, 42.02) * mm, v(-40.13, 40.89) * mm, v(-40, 39.63) * mm, v(-39.72, 39.02) * mm, v(-39.22, 38.41) * mm, v(-38.82, 38.01) * mm], "startDerivative": vector(-0.98, -5.74) * mm, "endDerivative": vector(2.9, -2.79) * mm});
            skFitSpline(sketch, "E155", {"points": [v(-38.82, 38.01) * mm, v(-39.2, 36.95) * mm, v(-39.9, 36.16) * mm, v(-40.7, 35.32) * mm, v(-41.7, 34.66) * mm], "startDerivative": vector(-1.13, -4.54) * mm, "endDerivative": vector(-4.01, -2.4) * mm});
            skFitSpline(sketch, "E156", {"points": [v(-37.36, 37.93) * mm, v(-36.68, 37.81) * mm, v(-35.96, 37.93) * mm, v(-35.35, 38.26) * mm, v(-35.01, 38.6) * mm], "startDerivative": vector(2.6, -0.6) * mm, "endDerivative": vector(1.4, 1.59) * mm});
            skFitSpline(sketch, "E157", {"points": [v(-35.01, 38.6) * mm, v(-36.27, 41.5) * mm, v(-36.34, 42.02) * mm, v(-36.1, 42.27) * mm], "startDerivative": vector(-2.74, 6.01) * mm, "endDerivative": vector(1.6, 1.2) * mm});
            skFitSpline(sketch, "E158", {"points": [v(-32.15, 41.73) * mm, v(-32.41, 42.58) * mm, v(-32.87, 43.06) * mm, v(-33.32, 43.44) * mm], "startDerivative": vector(-0.5, 2.48) * mm, "endDerivative": vector(-1.47, 1.22) * mm});
            skFitSpline(sketch, "E159", {"points": [v(-33.32, 43.44) * mm, v(-32.9, 44.09) * mm, v(-32.45, 45.26) * mm, v(-32.41, 46.74) * mm, v(-32.52, 48.02) * mm], "startDerivative": vector(2.04, 2.95) * mm, "endDerivative": vector(-0.47, 4.8) * mm});
            skLineSegment(sketch, "E160", {"start": v(-32.52, 48.02) * mm, "end": v(-36.76, 49.69) * mm});
            skLineSegment(sketch, "E161", {"start": v(-36.76, 49.69) * mm, "end": v(-39.9, 47.07) * mm});
            skFitSpline(sketch, "E162", {"points": [v(-24.11, 52.7) * mm, v(-23.67, 51.27) * mm, v(-23.43, 50.14) * mm, v(-23.28, 48.67) * mm, v(-23.28, 47.66) * mm], "startDerivative": vector(1.77, -5.5) * mm, "endDerivative": vector(-0.11, -4.32) * mm});
            skFitSpline(sketch, "E163", {"points": [v(-23.28, 47.66) * mm, v(-24.11, 48.23) * mm, v(-24.75, 48.62) * mm, v(-25.64, 48.67) * mm, v(-26.42, 48.23) * mm], "startDerivative": vector(-3.26, 2.26) * mm, "endDerivative": vector(-2.94, -2.17) * mm});
            skFitSpline(sketch, "E164", {"points": [v(-26.42, 48.23) * mm, v(-23.28, 45.39) * mm], "startDerivative": vector(3.14, -2.84) * mm, "endDerivative": vector(3.14, -2.84) * mm});
            skFitSpline(sketch, "E165", {"points": [v(-23.28, 45.39) * mm, v(-25.05, 45.2) * mm, v(-26.17, 44.2) * mm, v(-27.06, 43.52) * mm, v(-27.94, 42.84) * mm, v(-29.07, 41.51) * mm, v(-29.88, 41.2) * mm], "startDerivative": vector(-9.9, 0.32) * mm, "endDerivative": vector(-6.05, -1.15) * mm});
            skFitSpline(sketch, "E166", {"points": [v(-22.99, 44.06) * mm, v(-24.36, 39.6) * mm], "startDerivative": vector(-1.37, -4.46) * mm, "endDerivative": vector(-1.37, -4.46) * mm});
            skFitSpline(sketch, "E167", {"points": [v(-24.36, 39.6) * mm, v(-25.64, 40.19) * mm], "startDerivative": vector(-1.28, 0.59) * mm, "endDerivative": vector(-1.28, 0.59) * mm});
            skFitSpline(sketch, "E168", {"points": [v(-25.64, 40.19) * mm, v(-25, 40.73) * mm, v(-25.44, 40.97) * mm, v(-26.42, 40.87) * mm], "startDerivative": vector(2.78, 1.66) * mm, "endDerivative": vector(-2.65, -0.57) * mm});
            skFitSpline(sketch, "E169", {"points": [v(-26.42, 40.87) * mm, v(-26.08, 42.6) * mm], "startDerivative": vector(0.34, 1.72) * mm, "endDerivative": vector(0.34, 1.72) * mm});
            skFitSpline(sketch, "E170", {"points": [v(-26.08, 42.6) * mm, v(-25.4, 42.84) * mm, v(-24.36, 43.28) * mm, v(-23.53, 43.91) * mm, v(-22.99, 44.06) * mm], "startDerivative": vector(2.78, 1.02) * mm, "endDerivative": vector(2.63, 0.33) * mm});
            skFitSpline(sketch, "E171", {"points": [v(-21.14, 37.86) * mm, v(-20.89, 38.81) * mm, v(-20.57, 39.6) * mm, v(-20.12, 40.19) * mm, v(-19.3, 41.2) * mm, v(-18.34, 41.74) * mm, v(-17.39, 42) * mm], "startDerivative": vector(1.44, 5.79) * mm, "endDerivative": vector(5.74, 1.3) * mm});
            skFitSpline(sketch, "E172", {"points": [v(-17.39, 42) * mm, v(-17.39, 40.87) * mm, v(-17.96, 39.6) * mm, v(-18.92, 38.24) * mm], "startDerivative": vector(0.38, -3.7) * mm, "endDerivative": vector(-2.74, -3.7) * mm});
            skFitSpline(sketch, "E173", {"points": [v(-18.92, 38.24) * mm, v(-15.29, 37.73) * mm], "startDerivative": vector(3.63, -0.5) * mm, "endDerivative": vector(3.63, -0.5) * mm});
            skFitSpline(sketch, "E174", {"points": [v(-15.29, 37.73) * mm, v(-14.84, 39.13) * mm, v(-14.53, 40.87) * mm, v(-14.6, 42.25) * mm], "startDerivative": vector(1.41, 4.1) * mm, "endDerivative": vector(-0.44, 4.18) * mm});
            skFitSpline(sketch, "E175", {"points": [v(-14.6, 42.25) * mm, v(-14.22, 42.36) * mm, v(-13.78, 42.4) * mm, v(-12.99, 42.25) * mm], "startDerivative": vector(1.3, 0.42) * mm, "endDerivative": vector(2.08, -0.56) * mm});
            skFitSpline(sketch, "E176", {"points": [v(-12.99, 42.25) * mm, v(-13.21, 42.7) * mm, v(-13.54, 43.03) * mm, v(-13.96, 43.3) * mm, v(-14.68, 43.6) * mm, v(-14.7, 43.6) * mm], "startDerivative": vector(-0.84, 2.1) * mm, "endDerivative": vector(-0.24, -0.08) * mm});
            skFitSpline(sketch, "E177", {"points": [v(-14.7, 43.6) * mm, v(-14.7, 44.61) * mm, v(-14.7, 46.12) * mm, v(-15.18, 47.9) * mm, v(-15.74, 49.3) * mm, v(-16.42, 50.32) * mm], "startDerivative": vector(-0.12, 5.66) * mm, "endDerivative": vector(-3.87, 5.2) * mm});
            skFitSpline(sketch, "E178", {"points": [v(-16.42, 50.32) * mm, v(-17.82, 49.76) * mm, v(-19.49, 48.23) * mm, v(-20.96, 45.63) * mm, v(-22.02, 42.83) * mm, v(-22.29, 40.41) * mm, v(-22.22, 39.4) * mm, v(-21.95, 38.05) * mm], "startDerivative": vector(-11.25, -3.54) * mm, "endDerivative": vector(2.66, -12.14) * mm});
            skFitSpline(sketch, "E179", {"points": [v(-21.95, 38.05) * mm, v(-21.14, 37.86) * mm], "startDerivative": vector(0.8, -0.2) * mm, "endDerivative": vector(0.8, -0.2) * mm});
            skFitSpline(sketch, "E180", {"points": [v(-11.42, 47.93) * mm, v(-10.3, 47.66) * mm, v(-8.26, 47.02) * mm, v(-5.84, 45.96) * mm, v(-3.57, 44.82) * mm, v(-2.17, 43.53) * mm], "startDerivative": vector(8.92, -1.3) * mm, "endDerivative": vector(6.59, -7.12) * mm});
            skFitSpline(sketch, "E181", {"points": [v(-5.7, 41.55) * mm, v(-6.38, 42.25) * mm, v(-7.21, 42.8) * mm, v(-7.85, 43) * mm], "startDerivative": vector(-1.81, 2.03) * mm, "endDerivative": vector(-2.13, 0.48) * mm});
            skFitSpline(sketch, "E182", {"points": [v(-7.85, 43) * mm, v(-8.47, 41.8) * mm, v(-8.96, 40.66) * mm, v(-9.43, 38.94) * mm, v(-9.78, 37.54) * mm, v(-10.13, 36.09) * mm, v(-10.62, 34.01) * mm, v(-11.16, 32.04) * mm], "startDerivative": vector(-4.88, -9.45) * mm, "endDerivative": vector(-3.42, -12.09) * mm});
            skFitSpline(sketch, "E183", {"points": [v(-14.91, 32.87) * mm, v(-14.11, 35.22) * mm, v(-12.99, 37.86) * mm, v(-12.14, 39.6) * mm, v(-11.16, 41.55) * mm, v(-10.37, 43) * mm], "startDerivative": vector(3.42, 10.76) * mm, "endDerivative": vector(4.46, 7.98) * mm});
            skFitSpline(sketch, "E184", {"points": [v(-10.37, 43) * mm, v(-9.87, 43.8) * mm], "startDerivative": vector(0.5, 0.8) * mm, "endDerivative": vector(0.5, 0.8) * mm});
            skFitSpline(sketch, "E185", {"points": [v(-9.87, 43.8) * mm, v(-10.55, 44.23) * mm, v(-11.42, 44.43) * mm, v(-12.1, 44.43) * mm, v(-12.86, 44.43) * mm], "startDerivative": vector(-2.47, 1.87) * mm, "endDerivative": vector(-3.18, 0.04) * mm});
            skFitSpline(sketch, "E186", {"points": [v(-12.86, 44.43) * mm, v(-12.71, 44.68) * mm], "startDerivative": vector(0.15, 0.25) * mm, "endDerivative": vector(0.15, 0.25) * mm});
            skFitSpline(sketch, "E187", {"points": [v(-34.88, 20) * mm, v(-34, 18.15) * mm, v(-33.36, 15.67) * mm, v(-33.23, 13.32) * mm, v(-33.61, 10.65) * mm, v(-33.8, 10.01) * mm, v(-33.3, 9.88) * mm, v(-32.66, 11.03) * mm, v(-31.77, 12.94) * mm, v(-31.2, 15.1) * mm, v(-30.81, 17.9) * mm, v(-30.81, 17.9) * mm], "startDerivative": vector(8.99, -16.5) * mm, "endDerivative": vector(0.47, -1.23) * mm});
            skFitSpline(sketch, "E188", {"points": [v(-30.81, 17.9) * mm, v(-30.11, 16.96) * mm, v(-29.43, 14.62) * mm, v(-29.55, 11.78) * mm, v(-30.08, 9.81) * mm, v(-30.57, 8.38) * mm], "startDerivative": vector(4.67, -5.16) * mm, "endDerivative": vector(-2.76, -7.91) * mm});
            skFitSpline(sketch, "E189", {"points": [v(-30.57, 8.38) * mm, v(-31.21, 8.38) * mm, v(-31.82, 8.04) * mm, v(-32.8, 7.54) * mm], "startDerivative": vector(-2.24, 0.28) * mm, "endDerivative": vector(-2.7, -1.22) * mm});
            skFitSpline(sketch, "E190", {"points": [v(-32.8, 7.54) * mm, v(-33.48, 7.73) * mm, v(-34.5, 8.38) * mm], "startDerivative": vector(-1.52, 0.28) * mm, "endDerivative": vector(-1.87, 1.33) * mm});
            skFitSpline(sketch, "E191", {"points": [v(-34.5, 8.38) * mm, v(-34.96, 8.38) * mm, v(-35.6, 7.8) * mm, v(-36.85, 7.05) * mm], "startDerivative": vector(-1.92, 0.38) * mm, "endDerivative": vector(-3.18, -1.62) * mm});
            skFitSpline(sketch, "E192", {"points": [v(-36.85, 7.05) * mm, v(-37.75, 7.24) * mm, v(-39.08, 7.73) * mm, v(-39.87, 9.36) * mm, v(-40.52, 11.97) * mm, v(-40.74, 14.43) * mm, v(-40.25, 17.27) * mm, v(-39.27, 20.18) * mm, v(-37.8, 22.86) * mm, v(-36.05, 24.75) * mm, v(-33.78, 26.42) * mm, v(-31.59, 27.33) * mm], "startDerivative": vector(-14.6, 3.12) * mm, "endDerivative": vector(23.86, 8.24) * mm});
            skFitSpline(sketch, "E193", {"points": [v(-31.59, 27.33) * mm, v(-33.4, 25.93) * mm, v(-35.45, 23.96) * mm, v(-37.3, 19.84) * mm, v(-37.87, 16.32) * mm, v(-37.9, 13.22) * mm, v(-37.72, 10.88) * mm, v(-37.2, 9.68) * mm], "startDerivative": vector(-13.78, -10.6) * mm, "endDerivative": vector(6.2, -11.05) * mm});
            skFitSpline(sketch, "E194", {"points": [v(-37.2, 9.68) * mm, v(-36.73, 10.06) * mm, v(-36.44, 11.78) * mm, v(-35.83, 15.37) * mm, v(-35.27, 18.23) * mm, v(-34.88, 20) * mm], "startDerivative": vector(4.81, 2.5) * mm, "endDerivative": vector(2, 8.8) * mm});
            skFitSpline(sketch, "E195", {"points": [v(-25.6, 18.21) * mm, v(-27.33, 15.16) * mm, v(-27.82, 11.13) * mm, v(-27.33, 8.73) * mm, v(-26.08, 7.8) * mm, v(-24.36, 7.9) * mm, v(-22.38, 11.13) * mm, v(-22.42, 17.5) * mm], "startDerivative": vector(-13.34, -18.9) * mm, "endDerivative": vector(-3.72, 33.09) * mm});
            skFitSpline(sketch, "E196", {"points": [v(-25.17, 14.96) * mm, v(-25.86, 13.05) * mm, v(-25.64, 9.68) * mm, v(-25.17, 9.68) * mm, v(-24.36, 11.23) * mm, v(-24.36, 13.83) * mm, v(-25.17, 14.96) * mm]});
            skFitSpline(sketch, "E197", {"points": [v(-18.4, 10.16) * mm, v(-17.96, 12.76) * mm, v(-17.54, 16.23) * mm, v(-17.39, 18.73) * mm, v(-17.28, 22.62) * mm], "startDerivative": vector(1.9, 10.65) * mm, "endDerivative": vector(0.34, 14.9) * mm});
            skFitSpline(sketch, "E198", {"points": [v(-14.6, 7.25) * mm, v(-9.43, 6.18) * mm], "startDerivative": vector(5.16, -1.08) * mm, "endDerivative": vector(5.16, -1.08) * mm});
            skFitSpline(sketch, "E199", {"points": [v(-9.43, 6.18) * mm, v(-10.37, 8.38) * mm, v(-10.93, 12.06) * mm, v(-11.16, 15.35) * mm], "startDerivative": vector(-3.56, 6.88) * mm, "endDerivative": vector(-0.58, 9.26) * mm});
            skFitSpline(sketch, "E200", {"points": [v(-11.16, 15.35) * mm, v(-9.43, 15.7) * mm], "startDerivative": vector(1.74, 0.34) * mm, "endDerivative": vector(1.74, 0.34) * mm});
            skFitSpline(sketch, "E201", {"points": [v(-9.43, 15.7) * mm, v(-9.78, 16.53) * mm, v(-11.16, 17.5) * mm], "startDerivative": vector(-0.5, 2.04) * mm, "endDerivative": vector(-2.85, 1.6) * mm});
            skFitSpline(sketch, "E202", {"points": [v(-11.16, 17.5) * mm, v(-11.16, 19.08) * mm, v(-11.42, 21.97) * mm], "startDerivative": vector(0.1, 3.43) * mm, "endDerivative": vector(-0.58, 5.4) * mm});
            skFitSpline(sketch, "E203", {"points": [v(-11.42, 21.97) * mm, v(-10.37, 22.21) * mm, v(-8.97, 21.97) * mm], "startDerivative": vector(2.18, 0.76) * mm, "endDerivative": vector(2.72, -0.72) * mm});
            skFitSpline(sketch, "E204", {"points": [v(-8.97, 21.97) * mm, v(-9.1, 23.42) * mm, v(-9.2, 25.14) * mm, v(-9.23, 27.33) * mm], "startDerivative": vector(-0.52, 4.74) * mm, "endDerivative": vector(-0.04, 6.06) * mm});
            skFitSpline(sketch, "E205", {"points": [v(-9.23, 27.33) * mm, v(-10.22, 26.34) * mm, v(-11.42, 25.35) * mm, v(-12.86, 24.44) * mm, v(-14.7, 23.63) * mm], "startDerivative": vector(-4.19, -4.33) * mm, "endDerivative": vector(-6.92, -2.83) * mm});
            skFitSpline(sketch, "E206", {"points": [v(-14.7, 23.63) * mm, v(-14.11, 21.8) * mm, v(-13.4, 20) * mm, v(-12.71, 17.5) * mm], "startDerivative": vector(1.75, -5.9) * mm, "endDerivative": vector(1.77, -7.14) * mm});
            skFitSpline(sketch, "E207", {"points": [v(-12.71, 17.5) * mm, v(-13.65, 16.64) * mm, v(-14.46, 15.15) * mm], "startDerivative": vector(-2.14, -1.64) * mm, "endDerivative": vector(-1.37, -3.03) * mm});
            skFitSpline(sketch, "E208", {"points": [v(-14.46, 15.15) * mm, v(-12.86, 15.15) * mm], "startDerivative": vector(1.6, 0) * mm, "endDerivative": vector(1.6, 0) * mm});
            skFitSpline(sketch, "E209", {"points": [v(-12.86, 15.15) * mm, v(-12.71, 13.17) * mm, v(-12.99, 10.96) * mm, v(-13.63, 8.85) * mm, v(-14.6, 7.25) * mm], "startDerivative": vector(0.96, -7.98) * mm, "endDerivative": vector(-4.39, -6.38) * mm});
            skFitSpline(sketch, "E210", {"points": [v(-43.38, 27.75) * mm, v(-44.9, 27.33) * mm, v(-46.5, 26.58) * mm, v(-47.58, 25.97) * mm, v(-47.75, 25.8) * mm], "startDerivative": vector(-5.1, -1.18) * mm, "endDerivative": vector(-1.05, -1.37) * mm});
            skFitSpline(sketch, "E211", {"points": [v(-47.75, 25.8) * mm, v(-47.5, 26.36) * mm, v(-46.53, 27.82) * mm, v(-44.87, 30.22) * mm, v(-43.25, 32.25) * mm, v(-41.32, 34.1) * mm, v(-39.54, 35.4) * mm, v(-37.44, 36.6) * mm, v(-35.76, 37.25) * mm, v(-34.88, 37.46) * mm, v(-34.1, 38.47) * mm, v(-32.8, 40.03) * mm, v(-31.35, 41.55) * mm], "startDerivative": vector(4, 10.75) * mm, "endDerivative": vector(16.43, 16.99) * mm});
            skFitSpline(sketch, "E212", {"points": [v(-31.35, 41.55) * mm, v(-31.35, 40.87) * mm, v(-31.27, 39.4) * mm, v(-30.99, 38.24) * mm], "startDerivative": vector(-0.02, -2.27) * mm, "endDerivative": vector(0.92, -3.12) * mm});
            skFitSpline(sketch, "E213", {"points": [v(-30.99, 38.24) * mm, v(-30.57, 38.24) * mm], "startDerivative": vector(0.42, 0) * mm, "endDerivative": vector(0.42, 0) * mm});
            skFitSpline(sketch, "E214", {"points": [v(-30.57, 38.24) * mm, v(-30.07, 39.12) * mm, v(-28.72, 40.87) * mm, v(-26.98, 42.66) * mm], "startDerivative": vector(1.68, 3.31) * mm, "endDerivative": vector(4.55, 4.47) * mm});
            skFitSpline(sketch, "E215", {"points": [v(-26.98, 42.66) * mm, v(-27.17, 41.55) * mm, v(-27.33, 40.43) * mm, v(-27.3, 39.96) * mm, v(-26.86, 38.24) * mm, v(-26.67, 38.05) * mm], "startDerivative": vector(-0.82, -4.67) * mm, "endDerivative": vector(1.68, -0.85) * mm});
            skFitSpline(sketch, "E216", {"points": [v(-26.67, 38.05) * mm, v(-26.08, 37.95) * mm, v(-25.17, 37.7) * mm, v(-23.95, 37.18) * mm], "startDerivative": vector(2.12, -0.33) * mm, "endDerivative": vector(3.15, -1.45) * mm});
            skFitSpline(sketch, "E217", {"points": [v(-23.95, 37.18) * mm, v(-23.8, 37.46) * mm, v(-24.11, 38.48) * mm], "startDerivative": vector(0.6, 0.65) * mm, "endDerivative": vector(-0.8, 1.84) * mm});
            skFitSpline(sketch, "E218", {"points": [v(-24.11, 38.48) * mm, v(-23.28, 38.14) * mm, v(-22.32, 37.06) * mm, v(-21.33, 35.41) * mm], "startDerivative": vector(3.15, -0.9) * mm, "endDerivative": vector(2.45, -4.35) * mm});
            skFitSpline(sketch, "E219", {"points": [v(-21.33, 35.41) * mm, v(-20.93, 35.34) * mm, v(-20.57, 35.83) * mm, v(-21.33, 37.18) * mm], "startDerivative": vector(1.64, -0.7) * mm, "endDerivative": vector(-2.52, 3.11) * mm});
            skFitSpline(sketch, "E220", {"points": [v(-21.33, 37.18) * mm, v(-20.2, 36.82) * mm, v(-19.38, 35.41) * mm, v(-18.92, 33.53) * mm, v(-18.13, 32.2) * mm, v(-16.09, 31.34) * mm, v(-13.93, 30.66) * mm, v(-11.93, 30.17) * mm, v(-11.42, 29.6) * mm, v(-11.42, 28.88) * mm, v(-11.89, 28.28) * mm, v(-11.96, 27.9) * mm, v(-12.5, 27.52) * mm, v(-13.25, 27.33) * mm, v(-13.48, 26.87) * mm, v(-14.11, 26.87) * mm, v(-13.97, 26.58) * mm, v(-14.46, 26.08) * mm, v(-15.33, 25.25) * mm, v(-17.28, 24.6) * mm, v(-19.07, 24.27) * mm, v(-19.3, 23.96) * mm, v(-19.76, 23.32) * mm, v(-20.78, 22.86) * mm, v(-21.03, 22.86) * mm], "startDerivative": vector(26.73, -3.85) * mm, "endDerivative": vector(-9.64, 1.43) * mm});
            skFitSpline(sketch, "E221", {"points": [v(-21.03, 22.86) * mm, v(-20.85, 23.19) * mm, v(-20.57, 23.86) * mm, v(-20.57, 24.4) * mm, v(-20.7, 24.5) * mm], "startDerivative": vector(0.7, 1.25) * mm, "endDerivative": vector(-0.92, 0.37) * mm});
            skFitSpline(sketch, "E222", {"points": [v(-20.7, 24.5) * mm, v(-21.14, 24.25) * mm, v(-21.95, 23.75) * mm, v(-22.74, 22.86) * mm], "startDerivative": vector(-1.6, -0.9) * mm, "endDerivative": vector(-1.88, -2.47) * mm});
            skFitSpline(sketch, "E223", {"points": [v(-22.74, 22.86) * mm, v(-22.9, 23.19) * mm, v(-22.9, 23.63) * mm, v(-22.9, 23.98) * mm], "startDerivative": vector(-0.6, 0.94) * mm, "endDerivative": vector(-0.03, 1.05) * mm});
            skFitSpline(sketch, "E224", {"points": [v(-22.9, 23.87) * mm, v(-23.57, 23.46) * mm, v(-24.36, 22.38) * mm, v(-24.97, 21.16) * mm, v(-24.67, 19.67) * mm], "startDerivative": vector(-3.47, -1.55) * mm, "endDerivative": vector(1.93, -5.57) * mm});
            skFitSpline(sketch, "E225", {"points": [v(-24.67, 19.67) * mm, v(-25.17, 19.67) * mm, v(-25.84, 19.84) * mm, v(-26.42, 20.28) * mm], "startDerivative": vector(-1.62, -0.08) * mm, "endDerivative": vector(-1.53, 1.39) * mm});
            skFitSpline(sketch, "E226", {"points": [v(-26.42, 20.28) * mm, v(-26.98, 19.44) * mm, v(-27.7, 18.39) * mm, v(-28.4, 17.13) * mm], "startDerivative": vector(-1.79, -2.75) * mm, "endDerivative": vector(-1.88, -3.58) * mm});
            skFitSpline(sketch, "E227", {"points": [v(-28.4, 17.13) * mm, v(-29.08, 17.63) * mm, v(-30.07, 18.94) * mm, v(-30.99, 20.43) * mm], "startDerivative": vector(-2.54, 1.55) * mm, "endDerivative": vector(-2.36, 3.92) * mm});
            skFitSpline(sketch, "E228", {"points": [v(-30.99, 20.43) * mm, v(-31.35, 21.55) * mm], "startDerivative": vector(-0.36, 1.12) * mm, "endDerivative": vector(-0.36, 1.12) * mm});
            skFitSpline(sketch, "E229", {"points": [v(-31.35, 21.55) * mm, v(-31.9, 21.17) * mm, v(-32.19, 20) * mm, v(-32.32, 18.86) * mm], "startDerivative": vector(-2.23, -0.96) * mm, "endDerivative": vector(-0.36, -3.02) * mm});
            skFitSpline(sketch, "E230", {"points": [v(-32.32, 18.86) * mm, v(-33.18, 20.28) * mm, v(-33.93, 21.97) * mm, v(-34.5, 24.08) * mm, v(-33.67, 25.1) * mm, v(-31.97, 26.28) * mm, v(-30.34, 27.07) * mm, v(-29.13, 28.13) * mm], "startDerivative": vector(-6.54, 10.16) * mm, "endDerivative": vector(8.31, 8.51) * mm});
            skFitSpline(sketch, "E231", {"points": [v(-29.13, 28.13) * mm, v(-30.34, 28.13) * mm, v(-32.8, 27.71) * mm, v(-36.85, 25.6) * mm, v(-39.15, 22.3) * mm, v(-40.7, 18.86) * mm, v(-41.13, 16.49) * mm], "startDerivative": vector(-10.55, 0.3) * mm, "endDerivative": vector(-2.6, -14.41) * mm});
            skFitSpline(sketch, "E232", {"points": [v(-41.13, 16.49) * mm, v(-42.55, 16.72) * mm, v(-43.54, 16.49) * mm, v(-44.79, 15.7) * mm, v(-45.55, 14.1) * mm], "startDerivative": vector(-4.26, 1.98) * mm, "endDerivative": vector(-2.22, -6.17) * mm});
            skFitSpline(sketch, "E233", {"points": [v(-45.55, 14.1) * mm, v(-45.89, 15.7) * mm, v(-45.55, 17.9) * mm, v(-44.49, 20.28) * mm, v(-43.16, 22.42) * mm, v(-42.7, 23.17) * mm], "startDerivative": vector(-2.53, 8.23) * mm, "endDerivative": vector(2.8, 4.85) * mm});
            skFitSpline(sketch, "E234", {"points": [v(-42.7, 23.17) * mm, v(-43.88, 22.86) * mm, v(-45.24, 22.15) * mm, v(-47.48, 20) * mm], "startDerivative": vector(-4.37, -1) * mm, "endDerivative": vector(-5.4, -5.75) * mm});
            skFitSpline(sketch, "E235", {"points": [v(-47.48, 20) * mm, v(-47.32, 21.55) * mm, v(-46.3, 23.87) * mm, v(-44.64, 26.39) * mm, v(-43.38, 27.75) * mm], "startDerivative": vector(0.1, 7.12) * mm, "endDerivative": vector(5.39, 5.32) * mm});
            skFitSpline(sketch, "E236", {"points": [v(-29.13, 28.13) * mm, v(-27.68, 28.45) * mm, v(-25.6, 28.51) * mm, v(-25.6, 28.51) * mm], "startDerivative": vector(2.52, 0.84) * mm, "endDerivative": vector(-0.05, -0.08) * mm});
            skFitSpline(sketch, "E237", {"points": [v(-25.6, 28.51) * mm, v(-25.78, 28.72) * mm, v(-26.56, 29.2) * mm], "startDerivative": vector(-0.35, 0.56) * mm, "endDerivative": vector(-1.43, 0.8) * mm});
            skFitSpline(sketch, "E238", {"points": [v(-26.56, 29.2) * mm, v(-25.97, 29.59) * mm, v(-23.95, 30.3) * mm, v(-21.44, 30.94) * mm, v(-18.72, 30.78) * mm, v(-16.69, 30.35) * mm, v(-15.87, 29.7) * mm], "startDerivative": vector(4.63, 3.62) * mm, "endDerivative": vector(5.45, -5.6) * mm});
            skFitSpline(sketch, "E239", {"points": [v(-15.87, 29.7) * mm, v(-15.06, 29.7) * mm, v(-14, 29.8) * mm, v(-13.19, 29.7) * mm, v(-12.58, 29.2) * mm, v(-12.21, 28.4) * mm, v(-12.27, 27.9) * mm, v(-11.96, 27.9) * mm], "startDerivative": vector(5.13, -0.16) * mm, "endDerivative": vector(4.24, 0.8) * mm});
            skFitSpline(sketch, "E240", {"points": [v(-14.11, 26.87) * mm, v(-15.33, 27.07) * mm, v(-16.15, 27.33) * mm, v(-17.77, 27.51) * mm, v(-19.29, 27.51) * mm, v(-20.93, 27.51) * mm, v(-22.9, 26.87) * mm], "startDerivative": vector(-8.6, 1.13) * mm, "endDerivative": vector(-10.02, -4.21) * mm});
            skFitSpline(sketch, "E241", {"points": [v(-22.9, 26.87) * mm, v(-22.58, 27.9) * mm, v(-21.67, 29.2) * mm, v(-20.3, 29.7) * mm, v(-17.96, 29.44) * mm, v(-16.1, 28.51) * mm, v(-14.6, 27.33) * mm, v(-13.25, 27.33) * mm], "startDerivative": vector(1.99, 8.57) * mm, "endDerivative": vector(10.65, 1.96) * mm});
            skFitSpline(sketch, "E242", {"points": [v(-20.27, 33) * mm, v(-20.93, 33.03) * mm, v(-21.33, 33.09) * mm, v(-21.64, 33.58) * mm, v(-22.17, 34.31) * mm, v(-22.9, 35.1) * mm, v(-23.71, 35.22) * mm, v(-24.67, 35.22) * mm, v(-25.17, 35.22) * mm, v(-25.6, 35.53) * mm], "startDerivative": vector(-6.38, 0.44) * mm, "endDerivative": vector(-4.36, 4.1) * mm});
            skFitSpline(sketch, "E243", {"points": [v(-25.6, 35.53) * mm, v(-25.64, 35.28) * mm, v(-25.5, 34.99) * mm, v(-25.17, 34.7) * mm, v(-24.8, 34.72) * mm, v(-23.95, 34.67) * mm, v(-22.99, 34.33) * mm, v(-22.42, 33.66) * mm, v(-21.95, 32.94) * mm, v(-21.44, 32.67) * mm, v(-21.03, 32.42) * mm, v(-20.64, 32.35) * mm, v(-20.27, 33) * mm], "startDerivative": vector(-1.04, -4.56) * mm, "endDerivative": vector(3.37, 8.97) * mm});
            skFitSpline(sketch, "E244", {"points": [v(-21.33, 32.6) * mm, v(-21.58, 32.33) * mm, v(-21.9, 32.04) * mm, v(-22.42, 32.04) * mm, v(-23.52, 32.11) * mm, v(-24.36, 32.66) * mm, v(-25.03, 33.6) * mm, v(-25.03, 34.69) * mm], "startDerivative": vector(-2.4, -2.72) * mm, "endDerivative": vector(0.93, 6.57) * mm});
            skLineSegment(sketch, "E245", {"start": v(-5.7, 41.55) * mm, "end": v(-2.17, 43.53) * mm});
            skSolve(sketch);
        }
        {
            var Q0;
            Q0=makeQuery(id+"F2.imprint","IMPRINT",FACE,{"disambiguationData":[TD([[makeQuery(id+"F2.imprint","IMPRINT",EDGE,{"derivedFrom":sQuery(id+"F2.wireOp",EDGE,"E125")}),-1.0]])]});
            var Q1;
            Q1=makeQuery(id+"F2.imprint","IMPRINT",FACE,{"disambiguationData":[TD([[makeQuery(id+"F2.imprint","IMPRINT",EDGE,{"derivedFrom":sQuery(id+"F2.wireOp",EDGE,"E130")}),1.0]])]});
            var Q2;
            Q2=makeQuery(id+"F2.imprint","IMPRINT",FACE,{"disambiguationData":[TD([[makeQuery(id+"F2.imprint","IMPRINT",EDGE,{"derivedFrom":sQuery(id+"F2.wireOp",EDGE,"E136")}),1.0]])]});
            var Q3;
            Q3=makeQuery(id+"F2.imprint","IMPRINT",FACE,{"disambiguationData":[TD([[makeQuery(id+"F2.imprint","IMPRINT",EDGE,{"derivedFrom":sQuery(id+"F2.wireOp",EDGE,"E166")}),-1.0]])]});
            var Q4;
            Q4=makeQuery(id+"F2.imprint","IMPRINT",FACE,{"disambiguationData":[TD([[makeQuery(id+"F2.imprint","IMPRINT",EDGE,{"derivedFrom":sQuery(id+"F2.wireOp",EDGE,"E139")}),1.0]])]});
            var Q5;
            Q5=makeQuery(id+"F2.imprint","IMPRINT",FACE,{"disambiguationData":[TD([[makeQuery(id+"F2.imprint","IMPRINT",EDGE,{"derivedFrom":sQuery(id+"F2.wireOp",EDGE,"E142")}),1.0]])]});
            var Q6;
            Q6=makeQuery(id+"F2.imprint","IMPRINT",FACE,{"disambiguationData":[TD([[makeQuery(id+"F2.imprint","IMPRINT",EDGE,{"derivedFrom":sQuery(id+"F2.wireOp",EDGE,"E210")}),-1.0]])]});
            var Q7;
            Q7=makeQuery(id+"F2.imprint","IMPRINT",FACE,{"disambiguationData":[TD([[makeQuery(id+"F2.imprint","IMPRINT",EDGE,{"derivedFrom":sQuery(id+"F2.wireOp",EDGE,"E187")}),-1.0]])]});
            var Q8;
            Q8=makeQuery(id+"F2.imprint","IMPRINT",FACE,{"disambiguationData":[TD([[makeQuery(id+"F2.imprint","IMPRINT",EDGE,{"derivedFrom":sQuery(id+"F2.wireOp",EDGE,"E149")}),-1.0]])]});
            var Q9;
            Q9=makeQuery(id+"F2.imprint","IMPRINT",FACE,{"disambiguationData":[TD([[makeQuery(id+"F2.imprint","IMPRINT",EDGE,{"derivedFrom":sQuery(id+"F2.wireOp",EDGE,"E144")}),1.0]])]});
            var Q10;
            Q10=makeQuery(id+"F2.imprint","IMPRINT",FACE,{"disambiguationData":[TD([[makeQuery(id+"F2.imprint","IMPRINT",EDGE,{"derivedFrom":sQuery(id+"F2.wireOp",EDGE,"E198")}),1.0]])]});
            var Q11;
            {var subQ8=sQuery(id+"F2.wireOp",EDGE,"E221");Q11=makeQuery(id+"F2.imprint","IMPRINT",FACE,{"disambiguationData":[TD([[makeQuery(id+"F2.imprint","IMPRINT",EDGE,{"derivedFrom":subQ8}),-1.0]])]});}
            var Q12;
            {var subQ0=sQuery(id+"F2.wireOp",EDGE,"E240");Q12=makeQuery(id+"F2.imprint","IMPRINT",FACE,{"disambiguationData":[TD([[makeQuery(id+"F2.imprint","IMPRINT",EDGE,{"derivedFrom":subQ0}),-1.0]])]});}
            extrude(context, id + "F3", {"entities" : qUnion([Q0, Q1, Q2, Q3, Q4, Q5, Q6, Q7, Q8, Q9, Q10, Q11, Q12]), "operationType" : NewBodyOperationType.ADD, "depth" : 2 * mm});
        }
    });
